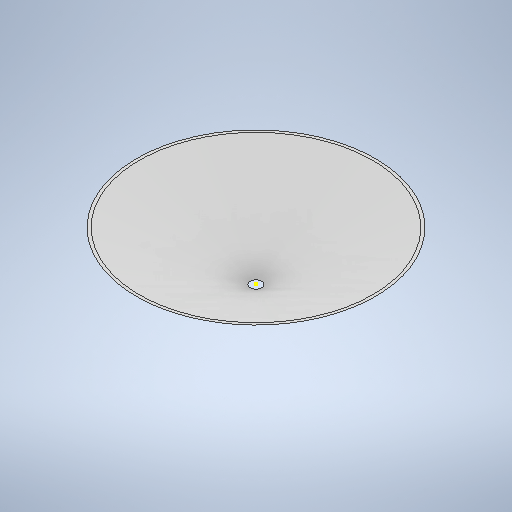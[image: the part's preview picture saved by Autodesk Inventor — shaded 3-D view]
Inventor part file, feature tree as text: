
AUTODESK INVENTOR PART (.ipt)
format: ipt  version: 2025 (Build 290162000, 162)  size: 243,712 bytes
history: native  units: mm
features: sketch x3, extrude x2, other x1
ambient origin geometry x8: Origin, YZ Plane, XZ Plane, XY Plane, X Axis, Y Axis, Z Axis, Center Point
bodies: Body1 (feature_tree)
feature tree (6):
  other  "Bryła1"
  extrude  "Wyciągnięcie proste1"  Depth=6.0mm
  sketch  "Szkic2"
  extrude  "Wyciągnięcie proste2"  Depth=40.0mm
  sketch  "Szkic1"
  sketch  "Szkic3"
